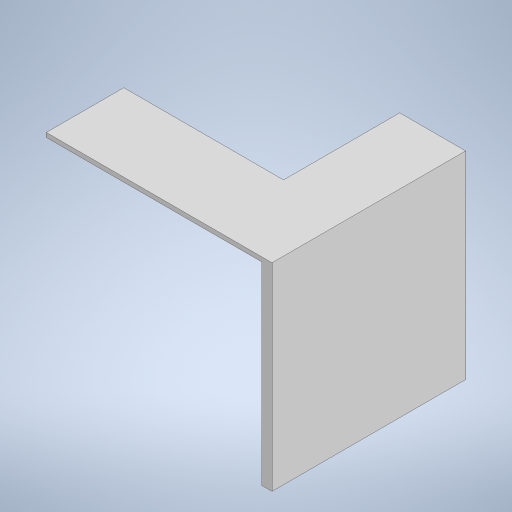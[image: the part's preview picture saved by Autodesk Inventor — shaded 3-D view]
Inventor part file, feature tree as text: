
AUTODESK INVENTOR PART (.ipt)
format: ipt  version: 2024 (Build 280153000, 153)  size: 322,560 bytes
history: native  units: mm
features: extrude x11, sketch x11
ambient origin geometry x8: Origin, YZ Plane, XZ Plane, XY Plane, X Axis, Y Axis, Z Axis, Center Point
bodies: Solid1 (feature_tree)
feature tree (22):
  extrude  "Top"  Depth=160.0mm
  extrude  "Right"  Depth=179.5mm
  extrude  "Left"  Depth=215.9mm
  extrude  "Plexiglass Cut"  Depth=25.4mm
  extrude  "Bottom"  Depth=50.8mm TaperAngle=0.0deg
  extrude  "Top Flattening"  Depth=50.8mm TaperAngle=0.0deg
  extrude  "Outer Side Flattening"  Depth=304.8mm TaperAngle=0.0deg
  extrude  "Bottom Flattening"  Depth=22.4mm TaperAngle=0.0deg
  extrude  "Inner Flattening"  Depth=22.389425mm
  extrude  "Bottom Cut"  Depth=22.4mm TaperAngle=0.0deg
  extrude  "Quarter Cut"  Depth=22.4mm TaperAngle=0.0deg
  sketch  "Sketch1"  dims[d11=220.0mm d12=160.0mm]
  sketch  "Sketch3"  dims[d15=248.6mm d16=179.5mm]
  sketch  "Sketch4"  dims[d18=304.8mm d19=215.9mm]
  sketch  "Sketch5"  dims[d20=25.4mm d21=0.0mm d22=25.4mm]
  sketch  "Sketch6"  dims[d25=266.7mm d26=50.8mm d27=0.0mm]
  sketch  "Sketch9"  dims[d28=266.7mm d29=50.8mm d30=0.0mm]
  sketch  "Sketch10"  dims[d31=12.7mm d32=304.8mm d33=0.0mm]
  sketch  "Sketch11"  dims[d34=25.4mm d35=0.0mm d46=22.4mm d47=0.0mm]
  sketch  "Sketch12"  dims[d48=22.389425mm d49=22.389425mm]
  sketch  "Sketch13"  dims[d50=0.0mm d51=0.0mm d52=22.4mm d53=0.0mm]
  sketch  "Sketch14"  dims[d54=296.8mm d55=22.4mm d56=0.0mm d57=0.0mm d58=0.0mm d59=0.0mm d60=0.0mm]
